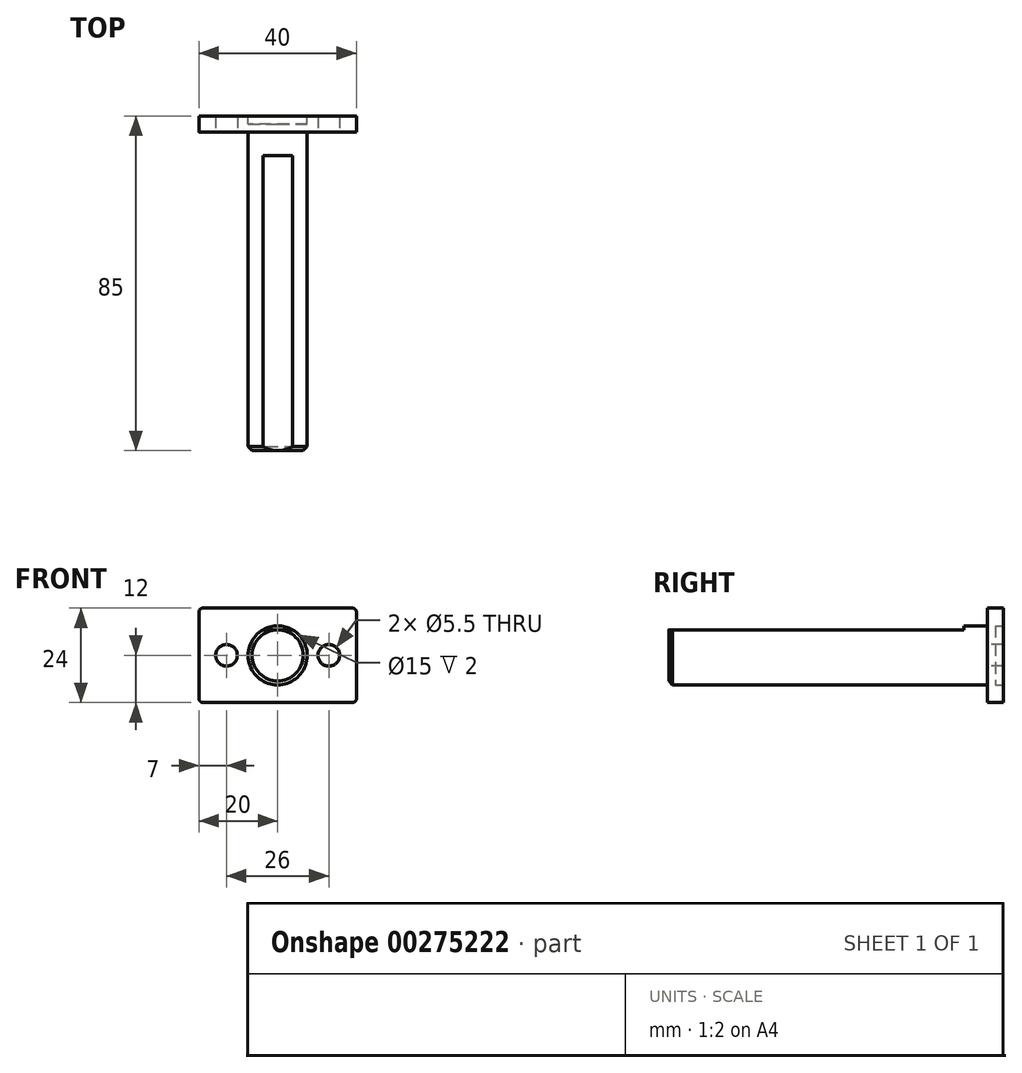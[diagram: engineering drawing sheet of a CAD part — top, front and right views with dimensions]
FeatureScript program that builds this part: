
annotation { "Feature Type Name" : "Feature", "Feature Type Description" : "" }
export const myFeature = defineFeature(function(context is Context, id is Id, definition is map)
    precondition{}
    {
        {
            var Q0;
            Q0=qCreatedBy(makeId("Front.planeOp"),FACE);
            var sketch = newSketch(context, id + "F0", { "sketchPlane" : qUnion([Q0])});
            skLineSegment(sketch, "E0.bottom", {"start": v(20, 12) * mm, "end": v(-20, 12) * mm});
            skLineSegment(sketch, "E0.top", {"start": v(20, -12) * mm, "end": v(-20, -12) * mm});
            skLineSegment(sketch, "E0.left", {"start": v(20, 12) * mm, "end": v(20, -12) * mm});
            skLineSegment(sketch, "E0.right", {"start": v(-20, 12) * mm, "end": v(-20, -12) * mm});
            skPoint(sketch, "E0.middle", {"position": v(0, 0) * mm});
            skCircle(sketch, "E1", {"center": v(0, 0) * mm, "radius": 7.5 * mm});
            skSolve(sketch);
        }
        {
            var Q0;
            Q0=makeQuery(id+"F0.imprint","IMPRINT",FACE,{"disambiguationData":[TD([[makeQuery(id+"F0.imprint","IMPRINT",EDGE,{"derivedFrom":sQuery(id+"F0.wireOp",EDGE,"E0.bottom")}),1.0]])]});
            extrude(context, id + "F1", {"entities" : qUnion([Q0]), "depth" : 4 * mm});
        }
        {
            var Q0;
            Q0=makeQuery(id+"F0.imprint","IMPRINT",FACE,{"disambiguationData":[TD([[makeQuery(id+"F0.imprint","IMPRINT",EDGE,{"derivedFrom":sQuery(id+"F0.wireOp",EDGE,"E1")}),1.0]])]});
            extrude(context, id + "F2", {"entities" : qUnion([Q0]), "operationType" : NewBodyOperationType.ADD, "depth" : 85 * mm});
        }
        {
            var Q0;
            Q0=makeQuery(id+"F1.opExtrude","CAP_FACE",FACE,{"disambiguationData":[OSD([sQuery(id+"F0.wireOp",EDGE,"E0.bottom"),sQuery(id+"F0.wireOp",EDGE,"E0.top"),sQuery(id+"F0.wireOp",EDGE,"E0.left"),sQuery(id+"F0.wireOp",EDGE,"E0.right"),sQuery(id+"F0.wireOp",EDGE,"E1")])],"isStart":false});
            var sketch = newSketch(context, id + "F3", { "sketchPlane" : qUnion([Q0])});
            skPoint(sketch, "E2", {"position": v(-13, 0) * mm});
            skPoint(sketch, "E3.MirrorP", {"position": v(13, 0) * mm});
            skSolve(sketch);
        }
        {
            var Q0;
            Q0=sQuery(id+"F3.wireOp",VERTEX,"E2");
            var Q1;
            Q1=sQuery(id+"F3.wireOp",VERTEX,"E3.MirrorP");
            var Q2;
            Q2=makeQuery(id+"F1.opExtrude","SWEPT_BODY",BODY,{"disambiguationData":[OSD([sQuery(id+"F0.wireOp",EDGE,"E0.bottom"),sQuery(id+"F0.wireOp",EDGE,"E0.top"),sQuery(id+"F0.wireOp",EDGE,"E0.left"),sQuery(id+"F0.wireOp",EDGE,"E0.right"),sQuery(id+"F0.wireOp",EDGE,"E1")])]});
            hole(context, id + "F4", {"style" : HoleStyle.SIMPLE, "endStyle" : HoleEndStyle.THROUGH, "standardTappedOrClearance" : lookupTablePath({ "standard" : "ISO", "fit" : "Normal", "size" : "M5", "type" : "Clearance" }), "standardBlindInLast" : lookupTablePath({ "fit" : "Standard", "standard" : "ISO", "size" : "M5", "type" : "Clearance" }), "holeDiameter" : 5.5 * mm, "tappedDepth" : 12 * mm, "tapClearance" : 3, "locations" : qUnion([Q0, Q1]), "scope" : qUnion([Q2])});
        }
        {
            var Q0;
            Q0=makeQuery(id+"F2.opExtrude","CAP_FACE",FACE,{"disambiguationData":[OSD([sQuery(id+"F0.wireOp",EDGE,"E1")])],"isStart":false});
            var sketch = newSketch(context, id + "F5", { "sketchPlane" : qUnion([Q0])});
            skLineSegment(sketch, "E4", {"start": v(-12.13, 6.5) * mm, "end": v(18.13, 6.5) * mm});
            skLineSegment(sketch, "E5", {"start": v(-12.13, 6.5) * mm, "end": v(8.5, 12.63) * mm});
            skLineSegment(sketch, "E6", {"start": v(8.5, 12.63) * mm, "end": v(18.13, 6.5) * mm});
            skSolve(sketch);
        }
        {
            var Q0;
            {var subQ0=sQuery(id+"F5.wireOp",EDGE,"E4");var subQ1=makeQuery(id+"F2.opExtrude","CAP_EDGE",EDGE,{"disambiguationData":[OSD([sQuery(id+"F0.wireOp",EDGE,"E1")])],"isStart":false});var subQ2=makeQuery(id+"F5.imprint","INTERSECT",VERTEX,{"disambiguationData":[OD(0.0)],"derivedFrom":[subQ1,subQ0]});Q0=makeQuery(id+"F5.imprint","IMPRINT",FACE,{"disambiguationData":[TD([[makeQuery(id+"F5.imprint","IMPRINT",EDGE,{"disambiguationData":[TD([[subQ2,-1.0]])],"derivedFrom":subQ0}),1.0]])]});}
            extrude(context, id + "F6", {"entities" : qUnion([Q0]), "operationType" : NewBodyOperationType.REMOVE, "oppositeDirection" : true, "depth" : 75 * mm});
        }
        {
            var Q0;
            Q0=makeQuery(id+"F1.opExtrude","SWEPT_EDGE",EDGE,{"disambiguationData":[OSD([sQuery(id+"F0.wireOp",EDGE,"E0.bottom"),sQuery(id+"F0.wireOp",EDGE,"E0.right")])]});
            var Q1;
            Q1=makeQuery(id+"F1.opExtrude","SWEPT_EDGE",EDGE,{"disambiguationData":[OSD([sQuery(id+"F0.wireOp",EDGE,"E0.bottom"),sQuery(id+"F0.wireOp",EDGE,"E0.left")])]});
            var Q2;
            Q2=makeQuery(id+"F1.opExtrude","SWEPT_EDGE",EDGE,{"disambiguationData":[OSD([sQuery(id+"F0.wireOp",EDGE,"E0.top"),sQuery(id+"F0.wireOp",EDGE,"E0.left")])]});
            var Q3;
            Q3=makeQuery(id+"F1.opExtrude","SWEPT_EDGE",EDGE,{"disambiguationData":[OSD([sQuery(id+"F0.wireOp",EDGE,"E0.top"),sQuery(id+"F0.wireOp",EDGE,"E0.right")])]});
            fillet(context, id + "F7", {"entities" : qUnion([Q0, Q1, Q2, Q3]), "radius" : 1 * mm, "tangentPropagation" : true, "allowEdgeOverflow" : false});
        }
        {
            var Q0;
            Q0=makeQuery(id+"F2.opExtrude","CAP_EDGE",EDGE,{"disambiguationData":[OSD([sQuery(id+"F0.wireOp",EDGE,"E1")])],"isStart":false});
            chamfer(context, id + "F8", {"entities" : qUnion([Q0]), "chamferType" : ChamferType.OFFSET_ANGLE, "width" : 1 * mm, "oppositeDirection" : false, "angle" : 45 * degree, "tangentPropagation" : true});
        }
        {
            var Q0;
            {var subQ0=sQuery(id+"F0.wireOp",EDGE,"E1");Q0=makeQuery(id+"F2.boolean.opBoolean","MERGE",FACE,{"derivedFrom":[makeQuery(id+"F1.opExtrude","CAP_FACE",FACE,{"disambiguationData":[OSD([sQuery(id+"F0.wireOp",EDGE,"E0.bottom"),sQuery(id+"F0.wireOp",EDGE,"E0.top"),sQuery(id+"F0.wireOp",EDGE,"E0.left"),sQuery(id+"F0.wireOp",EDGE,"E0.right"),subQ0])],"isStart":true}),makeQuery(id+"F2.opExtrude","CAP_FACE",FACE,{"disambiguationData":[OSD([subQ0])],"isStart":true})]});}
            var sketch = newSketch(context, id + "F9", { "sketchPlane" : qUnion([Q0])});
            skCircle(sketch, "E7", {"center": v(0, 0) * mm, "radius": 7.5 * mm});
            skSolve(sketch);
        }
        {
            var Q0;
            Q0=makeQuery(id+"F9.imprint","IMPRINT",FACE,{"disambiguationData":[TD([[makeQuery(id+"F9.imprint","IMPRINT",EDGE,{"derivedFrom":sQuery(id+"F9.wireOp",EDGE,"E7")}),1.0]])]});
            extrude(context, id + "F10", {"entities" : qUnion([Q0]), "operationType" : NewBodyOperationType.REMOVE, "oppositeDirection" : true, "depth" : 2 * mm});
        }
    });
